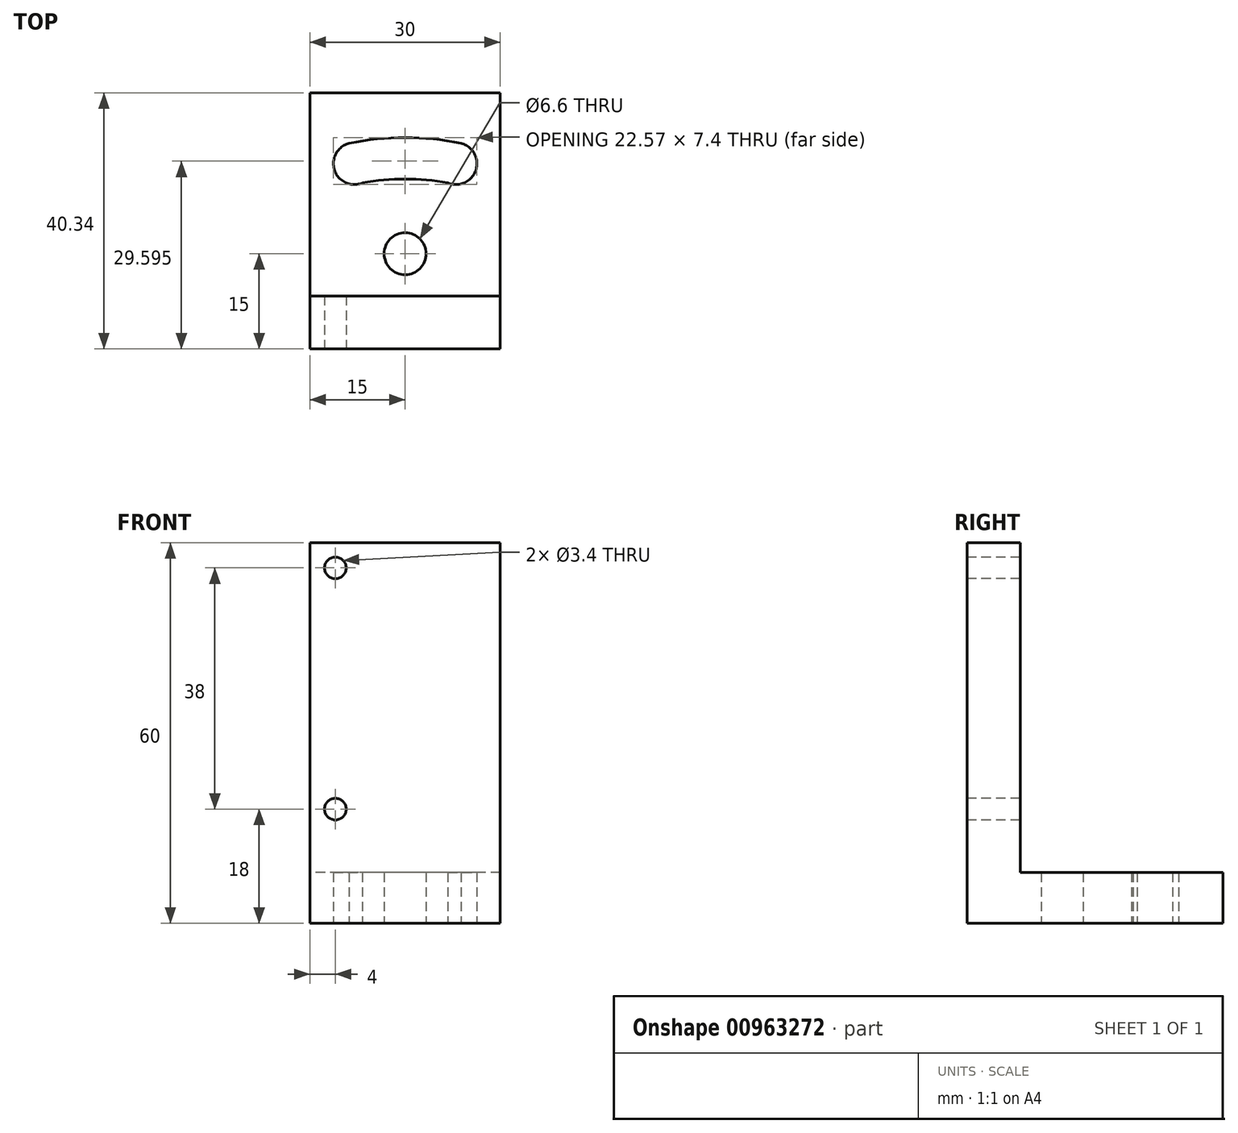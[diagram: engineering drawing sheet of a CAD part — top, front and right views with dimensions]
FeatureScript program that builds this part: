
annotation { "Feature Type Name" : "Feature", "Feature Type Description" : "" }
export const myFeature = defineFeature(function(context is Context, id is Id, definition is map)
    precondition{}
    {
        {
            var Q0;
            Q0=qCreatedBy(makeId("Right.planeOp"),FACE);
            var sketch = newSketch(context, id + "F0", { "sketchPlane" : qUnion([Q0])});
            skLineSegment(sketch, "E0", {"start": v(0, 0) * mm, "end": v(0, 60) * mm});
            skLineSegment(sketch, "E1", {"start": v(0, 60) * mm, "end": v(8.34, 60) * mm});
            skLineSegment(sketch, "E2", {"start": v(8.34, 60) * mm, "end": v(8.34, 8) * mm});
            skLineSegment(sketch, "E3", {"start": v(8.34, 8) * mm, "end": v(40.34, 8) * mm});
            skLineSegment(sketch, "E4", {"start": v(40.34, 8) * mm, "end": v(40.34, 0) * mm});
            skLineSegment(sketch, "E5", {"start": v(40.34, 0) * mm, "end": v(0, 0) * mm});
            skSolve(sketch);
        }
        {
            var Q0;
            Q0=makeQuery(id+"F0.imprint","IMPRINT",FACE,{"disambiguationData":[TD([[makeQuery(id+"F0.imprint","IMPRINT",EDGE,{"derivedFrom":sQuery(id+"F0.wireOp",EDGE,"E0")}),-1.0]])]});
            extrude(context, id + "F1", {"entities" : qUnion([Q0]), "depth" : 30 * mm, "offsetDistance" : 25 * mm});
        }
        {
            var Q0;
            Q0=makeQuery(id+"F1.opExtrude","SWEPT_FACE",FACE,{"disambiguationData":[OSD([sQuery(id+"F0.wireOp",EDGE,"E0")])]});
            var sketch = newSketch(context, id + "F2", { "sketchPlane" : qUnion([Q0])});
            skPoint(sketch, "E6", {"position": v(4, 56) * mm});
            skPoint(sketch, "E7", {"position": v(4, 18) * mm});
            skSolve(sketch);
        }
        {
            var Q0;
            Q0=sQuery(id+"F2.wireOp",VERTEX,"E6");
            var Q1;
            Q1=sQuery(id+"F2.wireOp",VERTEX,"E7");
            var Q2;
            Q2=makeQuery(id+"F1.opExtrude","SWEPT_BODY",BODY,{"disambiguationData":[OSD([sQuery(id+"F0.wireOp",EDGE,"E0"),sQuery(id+"F0.wireOp",EDGE,"E1"),sQuery(id+"F0.wireOp",EDGE,"E2"),sQuery(id+"F0.wireOp",EDGE,"E3"),sQuery(id+"F0.wireOp",EDGE,"E4"),sQuery(id+"F0.wireOp",EDGE,"E5")])]});
            hole(context, id + "F3", {"style" : HoleStyle.SIMPLE, "endStyle" : HoleEndStyle.THROUGH, "standardTappedOrClearance" : lookupTablePath({ "fit" : "Normal", "standard" : "ISO", "size" : "M3", "type" : "Clearance" }), "standardBlindInLast" : lookupTablePath({ "fit" : "Normal", "standard" : "ISO", "engagement" : "75%", "pitch" : "0.5 mm", "size" : "M3", "type" : "Clearance & tapped" }), "holeDiameter" : 3.4 * mm, "majorDiameter" : 6 * mm, "isTappedThrough" : true, "tappedDepth" : 12.6 * mm, "tapClearance" : 3, "startFromSketch" : true, "locations" : qUnion([Q0, Q1]), "scope" : qUnion([Q2])});
        }
        {
            var Q0;
            Q0=makeQuery(id+"F1.opExtrude","SWEPT_FACE",FACE,{"disambiguationData":[OSD([sQuery(id+"F0.wireOp",EDGE,"E5")])]});
            var sketch = newSketch(context, id + "F4", { "sketchPlane" : qUnion([Q0])});
            skPoint(sketch, "E8", {"position": v(15, -15) * mm});
            skPoint(sketch, "E8.positionSnap0", {"position": v(15, 0) * mm});
            skPoint(sketch, "E9", {"position": v(15, -30) * mm});
            skPoint(sketch, "E10", {"position": v(15, 10) * mm});
            skArc(sketch, "E11", {"start": v(3.8, -28.4) * mm, "mid": v(15, -30) * mm, "end": v(26.2, -28.4) * mm});
            skPoint(sketch, "E12", {"position": v(7, -29.2) * mm});
            skPoint(sketch, "E13", {"position": v(23, -29.2) * mm});
            skCircle(sketch, "E14", {"center": v(7, -29.2) * mm, "radius": 3.3 * mm});
            skCircle(sketch, "E15", {"center": v(23, -29.2) * mm, "radius": 3.3 * mm});
            skArc(sketch, "E16", {"start": v(7.02, -25.9) * mm, "mid": v(15, -26.77) * mm, "end": v(22.98, -25.9) * mm});
            skArc(sketch, "E17", {"start": v(6.2, -32.4) * mm, "mid": v(15, -33.3) * mm, "end": v(23.8, -32.4) * mm});
            skSolve(sketch);
        }
        {
            var Q0;
            {var subQ0=sQuery(id+"F4.wireOp",EDGE,"E16");var subQ1=sQuery(id+"F4.wireOp",EDGE,"E14");var subQ2=makeQuery(id+"F4.imprint","INTERSECT",VERTEX,{"disambiguationData":[OD(0.0)],"derivedFrom":[subQ1,subQ0]});Q0=makeQuery(id+"F4.imprint","IMPRINT",FACE,{"disambiguationData":[TD([[makeQuery(id+"F4.imprint","IMPRINT",EDGE,{"disambiguationData":[TD([[subQ2,1.0]])],"derivedFrom":subQ1}),1.0]])]});}
            var Q1;
            {var subQ0=sQuery(id+"F4.wireOp",EDGE,"E43I8wlD-Lmg6-5iig-6DMm-U61DjmO3cmHz");var subQ1=sQuery(id+"F4.wireOp",EDGE,"E14");var subQ2=makeQuery(id+"F4.imprint","INTERSECT",VERTEX,{"disambiguationData":[OD(0.0)],"derivedFrom":[subQ1,subQ0]});Q1=makeQuery(id+"F4.imprint","IMPRINT",FACE,{"disambiguationData":[TD([[makeQuery(id+"F4.imprint","IMPRINT",EDGE,{"disambiguationData":[TD([[subQ2,-1.0]])],"derivedFrom":subQ1}),1.0]])]});}
            var Q2;
            {var subQ0=sQuery(id+"F4.wireOp",EDGE,"E16");var subQ1=sQuery(id+"F4.wireOp",EDGE,"E15");var subQ2=makeQuery(id+"F4.imprint","INTERSECT",VERTEX,{"disambiguationData":[OD(0.0)],"derivedFrom":[subQ1,subQ0]});Q2=makeQuery(id+"F4.imprint","IMPRINT",FACE,{"disambiguationData":[TD([[makeQuery(id+"F4.imprint","IMPRINT",EDGE,{"disambiguationData":[TD([[subQ2,-1.0]])],"derivedFrom":subQ1}),1.0]])]});}
            var Q3;
            {var subQ0=sQuery(id+"F4.wireOp",EDGE,"E43I8wlD-Lmg6-5iig-6DMm-U61DjmO3cmHz");var subQ1=sQuery(id+"F4.wireOp",EDGE,"E15");var subQ2=makeQuery(id+"F4.imprint","INTERSECT",VERTEX,{"disambiguationData":[OD(0.0)],"derivedFrom":[subQ1,subQ0]});Q3=makeQuery(id+"F4.imprint","IMPRINT",FACE,{"disambiguationData":[TD([[makeQuery(id+"F4.imprint","IMPRINT",EDGE,{"disambiguationData":[TD([[subQ2,1.0]])],"derivedFrom":subQ1}),1.0]])]});}
            var Q4;
            {var subQ0=sQuery(id+"F4.wireOp",EDGE,"E14");var subQ1=sQuery(id+"F4.wireOp",EDGE,"E11");var subQ2=makeQuery(id+"F4.imprint","INTERSECT",VERTEX,{"disambiguationData":[OD(1.0)],"derivedFrom":[subQ1,subQ0]});Q4=makeQuery(id+"F4.imprint","IMPRINT",FACE,{"disambiguationData":[TD([[makeQuery(id+"F4.imprint","IMPRINT",EDGE,{"disambiguationData":[TD([[subQ2,-1.0]])],"derivedFrom":subQ1}),-1.0]])]});}
            var Q5;
            {var subQ0=sQuery(id+"F4.wireOp",EDGE,"E14");var subQ1=sQuery(id+"F4.wireOp",EDGE,"E11");var subQ2=makeQuery(id+"F4.imprint","INTERSECT",VERTEX,{"disambiguationData":[OD(1.0)],"derivedFrom":[subQ1,subQ0]});Q5=makeQuery(id+"F4.imprint","IMPRINT",FACE,{"disambiguationData":[TD([[makeQuery(id+"F4.imprint","IMPRINT",EDGE,{"disambiguationData":[TD([[subQ2,-1.0]])],"derivedFrom":subQ1}),1.0]])]});}
            var Q6;
            {var subQ0=sQuery(id+"F4.wireOp",EDGE,"E14");var subQ1=sQuery(id+"F4.wireOp",EDGE,"E11");var subQ2=makeQuery(id+"F4.imprint","INTERSECT",VERTEX,{"disambiguationData":[OD(0.0)],"derivedFrom":[subQ1,subQ0]});Q6=makeQuery(id+"F4.imprint","IMPRINT",FACE,{"disambiguationData":[TD([[makeQuery(id+"F4.imprint","IMPRINT",EDGE,{"disambiguationData":[TD([[subQ2,-1.0]])],"derivedFrom":subQ1}),1.0]])]});}
            var Q7;
            {var subQ0=sQuery(id+"F4.wireOp",EDGE,"E14");var subQ1=sQuery(id+"F4.wireOp",EDGE,"E11");var subQ2=makeQuery(id+"F4.imprint","INTERSECT",VERTEX,{"disambiguationData":[OD(0.0)],"derivedFrom":[subQ1,subQ0]});Q7=makeQuery(id+"F4.imprint","IMPRINT",FACE,{"disambiguationData":[TD([[makeQuery(id+"F4.imprint","IMPRINT",EDGE,{"disambiguationData":[TD([[subQ2,-1.0]])],"derivedFrom":subQ1}),-1.0]])]});}
            var Q8;
            {var subQ0=sQuery(id+"F4.wireOp",EDGE,"E15");var subQ1=sQuery(id+"F4.wireOp",EDGE,"E11");var subQ2=makeQuery(id+"F4.imprint","INTERSECT",VERTEX,{"disambiguationData":[OD(0.0)],"derivedFrom":[subQ1,subQ0]});Q8=makeQuery(id+"F4.imprint","IMPRINT",FACE,{"disambiguationData":[TD([[makeQuery(id+"F4.imprint","IMPRINT",EDGE,{"disambiguationData":[TD([[subQ2,1.0]])],"derivedFrom":subQ1}),-1.0]])]});}
            var Q9;
            {var subQ0=sQuery(id+"F4.wireOp",EDGE,"E15");var subQ1=sQuery(id+"F4.wireOp",EDGE,"E11");var subQ2=makeQuery(id+"F4.imprint","INTERSECT",VERTEX,{"disambiguationData":[OD(0.0)],"derivedFrom":[subQ1,subQ0]});Q9=makeQuery(id+"F4.imprint","IMPRINT",FACE,{"disambiguationData":[TD([[makeQuery(id+"F4.imprint","IMPRINT",EDGE,{"disambiguationData":[TD([[subQ2,1.0]])],"derivedFrom":subQ1}),1.0]])]});}
            extrude(context, id + "F5", {"entities" : qUnion([Q0, Q1, Q2, Q3, Q4, Q5, Q6, Q7, Q8, Q9]), "operationType" : NewBodyOperationType.REMOVE, "oppositeDirection" : true, "depth" : 25 * mm, "offsetDistance" : 25 * mm});
        }
        {
            var Q0;
            Q0=sQuery(id+"F4.wireOp",VERTEX,"E8");
            var Q1;
            Q1=makeQuery(id+"F1.opExtrude","SWEPT_BODY",BODY,{"disambiguationData":[OSD([sQuery(id+"F0.wireOp",EDGE,"E0"),sQuery(id+"F0.wireOp",EDGE,"E1"),sQuery(id+"F0.wireOp",EDGE,"E2"),sQuery(id+"F0.wireOp",EDGE,"E3"),sQuery(id+"F0.wireOp",EDGE,"E4"),sQuery(id+"F0.wireOp",EDGE,"E5")])]});
            hole(context, id + "F6", {"style" : HoleStyle.SIMPLE, "endStyle" : HoleEndStyle.THROUGH, "standardTappedOrClearance" : lookupTablePath({ "fit" : "Normal", "standard" : "ISO", "size" : "M6", "type" : "Clearance" }), "standardBlindInLast" : lookupTablePath({ "fit" : "Normal", "standard" : "ISO", "engagement" : "75%", "pitch" : "1 mm", "size" : "M6", "type" : "Clearance & tapped" }), "holeDiameter" : 6.6 * mm, "majorDiameter" : 5 * mm, "isTappedThrough" : true, "tappedDepth" : 12.6 * mm, "tapClearance" : 3, "startFromSketch" : true, "locations" : qUnion([Q0]), "scope" : qUnion([Q1])});
        }
    });
